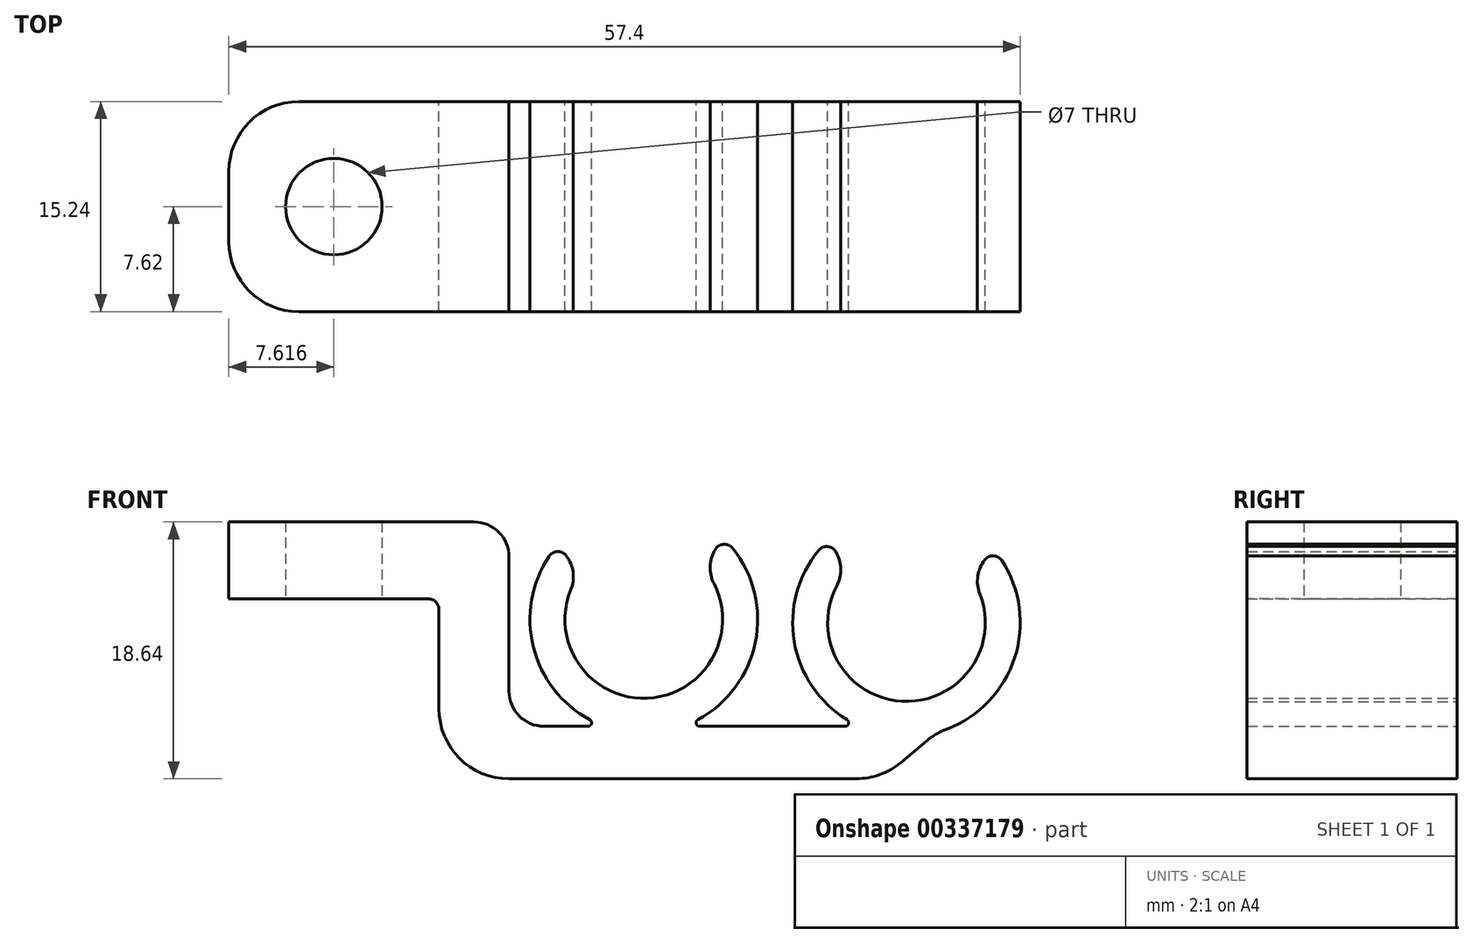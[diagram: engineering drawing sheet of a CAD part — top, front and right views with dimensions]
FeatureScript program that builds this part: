
annotation { "Feature Type Name" : "Feature", "Feature Type Description" : "" }
export const myFeature = defineFeature(function(context is Context, id is Id, definition is map)
    precondition{}
    {
        {
            var Q0;
            Q0=qCreatedBy(makeId("Front.planeOp"),FACE);
            var sketch = newSketch(context, id + "F0", { "sketchPlane" : qUnion([Q0])});
            skArc(sketch, "E0", {"start": v(-13.9, 13.2) * mm, "mid": v(-9.28, 3.82) * mm, "end": v(-5.48, 13.57) * mm});
            skArc(sketch, "E1", {"start": v(5.53, 13.38) * mm, "mid": v(9.2, 3.59) * mm, "end": v(13.95, 12.92) * mm});
            skArc(sketch, "E2", {"start": v(-15.85, 14.83) * mm, "mid": v(-9.16, 1.28) * mm, "end": v(-3.69, 15.36) * mm});
            skArc(sketch, "E3", {"start": v(3.76, 15.2) * mm, "mid": v(9.06, 1.05) * mm, "end": v(15.91, 14.53) * mm});
            skLineSegment(sketch, "E4", {"start": v(-9.53, 9.52) * mm, "end": v(0, 19.05) * mm, "construction": true});
            skLineSegment(sketch, "E5", {"start": v(0, 19.05) * mm, "end": v(9.52, 9.3) * mm, "construction": true});
            skLineSegment(sketch, "E6", {"start": v(-9.52, 9.52) * mm, "end": v(-20.75, 18.95) * mm, "construction": true});
            skLineSegment(sketch, "E7", {"start": v(9.52, 9.3) * mm, "end": v(20.07, 17.93) * mm, "construction": true});
            skLineSegment(sketch, "E8", {"start": v(-15.85, 14.83) * mm, "end": v(-13.9, 13.2) * mm});
            skLineSegment(sketch, "E9", {"start": v(-5.48, 13.57) * mm, "end": v(-3.69, 15.36) * mm});
            skLineSegment(sketch, "E10", {"start": v(3.76, 15.2) * mm, "end": v(5.53, 13.38) * mm});
            skLineSegment(sketch, "E11", {"start": v(13.95, 12.92) * mm, "end": v(15.91, 14.53) * mm});
            skSolve(sketch);
        }
        {
            var Q0;
            Q0 = qSketchRegion(id + "F0", true);
            extrude(context, id + "F1", {"entities" : qUnion([Q0]), "depth" : 15.24 * mm});
        }
        {
            var Q0;
            Q0=qCreatedBy(makeId("Front.planeOp"),FACE);
            var sketch = newSketch(context, id + "F2", { "sketchPlane" : qUnion([Q0])});
            skLineSegment(sketch, "E12", {"start": v(-19.3, 1.78) * mm, "end": v(12.25, 1.78) * mm});
            skLineSegment(sketch, "E13", {"start": v(-24.38, -2.03) * mm, "end": v(7.71, -2.03) * mm});
            skLineSegment(sketch, "E14", {"start": v(7.71, -2.03) * mm, "end": v(12.25, 1.78) * mm});
            skLineSegment(sketch, "E15", {"start": v(-19.3, 1.78) * mm, "end": v(-19.3, 16.6) * mm});
            skLineSegment(sketch, "E16", {"start": v(-19.3, 16.6) * mm, "end": v(-39.62, 16.6) * mm});
            skLineSegment(sketch, "E17", {"start": v(-39.62, 16.6) * mm, "end": v(-39.62, 11.02) * mm});
            skLineSegment(sketch, "E18", {"start": v(-39.62, 11.02) * mm, "end": v(-24.38, 11.02) * mm});
            skLineSegment(sketch, "E19", {"start": v(-24.38, 11.02) * mm, "end": v(-24.38, -2.03) * mm});
            skSolve(sketch);
        }
        {
            var Q0;
            Q0 = qSketchRegion(id + "F2", true);
            extrude(context, id + "F3", {"entities" : qUnion([Q0]), "operationType" : NewBodyOperationType.ADD, "depth" : 15.24 * mm});
        }
        {
            var Q0;
            Q0=makeQuery(id+"F3.opExtrude","SWEPT_FACE",FACE,{"disambiguationData":[OSD([sQuery(id+"F2.wireOp",EDGE,"E18")])]});
            var sketch = newSketch(context, id + "F4", { "sketchPlane" : qUnion([Q0])});
            skPoint(sketch, "E20", {"position": v(-32, 7.62) * mm});
            skPoint(sketch, "E20.positionSnap0", {"position": v(-32, 15.24) * mm});
            skSolve(sketch);
        }
        {
            var Q0;
            Q0=sQuery(id+"F4.wireOp",VERTEX,"E20");
            var Q1;
            Q1=makeQuery(id+"F1.opExtrude","SWEPT_BODY",BODY,{"disambiguationData":[OSD([sQuery(id+"F0.wireOp",EDGE,"E0"),sQuery(id+"F0.wireOp",EDGE,"E2"),sQuery(id+"F0.wireOp",EDGE,"E8"),sQuery(id+"F0.wireOp",EDGE,"E9")])]});
            hole(context, id + "F5", {"style" : HoleStyle.SIMPLE, "endStyle" : HoleEndStyle.THROUGH, "holeDiameter" : 7 * mm, "tappedDepth" : 12.7 * mm, "tapClearance" : 3, "locations" : qUnion([Q0]), "scope" : qUnion([Q1])});
        }
        {
            var Q0;
            Q0=makeQuery(id+"F3.opExtrude","CAP_EDGE",EDGE,{"disambiguationData":[OSD([sQuery(id+"F2.wireOp",EDGE,"E17")])],"isStart":false});
            var Q1;
            Q1=makeQuery(id+"F3.opExtrude","CAP_EDGE",EDGE,{"disambiguationData":[OSD([sQuery(id+"F2.wireOp",EDGE,"E17")])],"isStart":true});
            var Q2;
            Q2=makeQuery(id+"F3.opExtrude","SWEPT_EDGE",EDGE,{"disambiguationData":[OSD([sQuery(id+"F2.wireOp",EDGE,"E13"),sQuery(id+"F2.wireOp",EDGE,"E19")])]});
            var Q3;
            Q3=makeQuery(id+"F3.boolean.opBoolean","INTERSECT",EDGE,{"derivedFrom":[makeQuery(id+"F1.opExtrude","SWEPT_FACE",FACE,{"disambiguationData":[OSD([sQuery(id+"F0.wireOp",EDGE,"E3")])]}),makeQuery(id+"F3.opExtrude","SWEPT_FACE",FACE,{"disambiguationData":[OSD([sQuery(id+"F2.wireOp",EDGE,"E14")])]})]});
            var Q4;
            Q4=makeQuery(id+"F3.opExtrude","SWEPT_EDGE",EDGE,{"disambiguationData":[OSD([sQuery(id+"F2.wireOp",EDGE,"E13"),sQuery(id+"F2.wireOp",EDGE,"E14")])]});
            fillet(context, id + "F6", {"entities" : qUnion([Q0, Q1, Q2, Q3, Q4]), "radius" : 5.08 * mm, "tangentPropagation" : true, "allowEdgeOverflow" : false});
        }
        {
            var Q0;
            Q0=makeQuery(id+"F3.opExtrude","SWEPT_EDGE",EDGE,{"disambiguationData":[OSD([sQuery(id+"F2.wireOp",EDGE,"E15"),sQuery(id+"F2.wireOp",EDGE,"E16")])]});
            var Q1;
            Q1=makeQuery(id+"F3.opExtrude","SWEPT_EDGE",EDGE,{"disambiguationData":[OSD([sQuery(id+"F2.wireOp",EDGE,"E12"),sQuery(id+"F2.wireOp",EDGE,"E15")])]});
            var Q2;
            Q2=makeQuery(id+"F1.opExtrude","SWEPT_EDGE",EDGE,{"disambiguationData":[OSD([sQuery(id+"F0.wireOp",EDGE,"E0"),sQuery(id+"F0.wireOp",EDGE,"E8")])]});
            var Q3;
            Q3=makeQuery(id+"F1.opExtrude","SWEPT_EDGE",EDGE,{"disambiguationData":[OSD([sQuery(id+"F0.wireOp",EDGE,"E0"),sQuery(id+"F0.wireOp",EDGE,"E9")])]});
            var Q4;
            Q4=makeQuery(id+"F1.opExtrude","SWEPT_EDGE",EDGE,{"disambiguationData":[OSD([sQuery(id+"F0.wireOp",EDGE,"E1"),sQuery(id+"F0.wireOp",EDGE,"E10")])]});
            var Q5;
            Q5=makeQuery(id+"F1.opExtrude","SWEPT_EDGE",EDGE,{"disambiguationData":[OSD([sQuery(id+"F0.wireOp",EDGE,"E1"),sQuery(id+"F0.wireOp",EDGE,"E11")])]});
            fillet(context, id + "F7", {"entities" : qUnion([Q0, Q1, Q2, Q3, Q4, Q5]), "radius" : 2.54 * mm, "tangentPropagation" : true, "allowEdgeOverflow" : false});
        }
        {
            var Q0;
            Q0=makeQuery(id+"F1.opExtrude","SWEPT_EDGE",EDGE,{"disambiguationData":[OSD([sQuery(id+"F0.wireOp",EDGE,"E2"),sQuery(id+"F0.wireOp",EDGE,"E8")])]});
            var Q1;
            Q1=makeQuery(id+"F1.opExtrude","SWEPT_EDGE",EDGE,{"disambiguationData":[OSD([sQuery(id+"F0.wireOp",EDGE,"E2"),sQuery(id+"F0.wireOp",EDGE,"E9")])]});
            var Q2;
            Q2=makeQuery(id+"F1.opExtrude","SWEPT_EDGE",EDGE,{"disambiguationData":[OSD([sQuery(id+"F0.wireOp",EDGE,"E3"),sQuery(id+"F0.wireOp",EDGE,"E10")])]});
            var Q3;
            Q3=makeQuery(id+"F1.opExtrude","SWEPT_EDGE",EDGE,{"disambiguationData":[OSD([sQuery(id+"F0.wireOp",EDGE,"E3"),sQuery(id+"F0.wireOp",EDGE,"E11")])]});
            var Q4;
            Q4=makeQuery(id+"F3.opExtrude","SWEPT_EDGE",EDGE,{"disambiguationData":[OSD([sQuery(id+"F2.wireOp",EDGE,"E18"),sQuery(id+"F2.wireOp",EDGE,"E19")])]});
            fillet(context, id + "F8", {"entities" : qUnion([Q0, Q1, Q2, Q3, Q4]), "radius" : 0.76 * mm, "tangentPropagation" : true, "allowEdgeOverflow" : false});
        }
        {
            var Q0;
            Q0=makeQuery(id+"F3.boolean.opBoolean","INTERSECT",EDGE,{"disambiguationData":[OD(0.0)],"derivedFrom":[makeQuery(id+"F1.opExtrude","SWEPT_FACE",FACE,{"disambiguationData":[OSD([sQuery(id+"F0.wireOp",EDGE,"E2")])]}),makeQuery(id+"F3.opExtrude","SWEPT_FACE",FACE,{"disambiguationData":[OSD([sQuery(id+"F2.wireOp",EDGE,"E12")])]})]});
            var Q1;
            Q1=makeQuery(id+"F3.boolean.opBoolean","INTERSECT",EDGE,{"disambiguationData":[OD(1.0)],"derivedFrom":[makeQuery(id+"F1.opExtrude","SWEPT_FACE",FACE,{"disambiguationData":[OSD([sQuery(id+"F0.wireOp",EDGE,"E2")])]}),makeQuery(id+"F3.opExtrude","SWEPT_FACE",FACE,{"disambiguationData":[OSD([sQuery(id+"F2.wireOp",EDGE,"E12")])]})]});
            var Q2;
            Q2=makeQuery(id+"F3.boolean.opBoolean","INTERSECT",EDGE,{"derivedFrom":[makeQuery(id+"F1.opExtrude","SWEPT_FACE",FACE,{"disambiguationData":[OSD([sQuery(id+"F0.wireOp",EDGE,"E3")])]}),makeQuery(id+"F3.opExtrude","SWEPT_FACE",FACE,{"disambiguationData":[OSD([sQuery(id+"F2.wireOp",EDGE,"E12")])]})]});
            fillet(context, id + "F9", {"entities" : qUnion([Q0, Q1, Q2]), "radius" : 0.25 * mm, "tangentPropagation" : true, "allowEdgeOverflow" : false});
        }
    });
